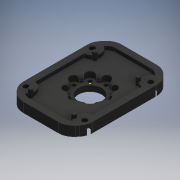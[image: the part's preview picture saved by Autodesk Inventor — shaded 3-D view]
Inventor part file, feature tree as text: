
AUTODESK INVENTOR PART (.ipt)
format: ipt  version: 2019 (Build 230136000, 136)  size: 553,984 bytes
history: native  units: mm
features: extrude x8, sketch x4, other x2, fillet x2, pattern_circular x2, shell x1, chamfer x1, pattern_linear x1
ambient origin geometry x8: Origin, YZ Plane, XZ Plane, XY Plane, X Axis, Y Axis, Z Axis, Center Point
bodies: Solid1 (feature_tree)
feature tree (21):
  other  "connector"
  sketch  "Sketch1"  dims[d1=20.0mm d3=20.0mm d4=30.0mm d5=17.0mm d6=5.0mm d7=0.0mm d8=8.0mm d9=22.0mm]
  extrude  "Extrusion1"  Depth=8.0mm
  fillet  "Fillet1"  Radius=22.0mm
  extrude  "Extrusion4"  Depth=3.0mm TaperAngle=0.0deg
  shell  "Shell2"  Thickness=0.5mm
  sketch  "Sketch2"  dims[d14=0.5mm d15=1.0mm d16=0.0mm]
  extrude  "Extrusion2"  Depth=1.0mm TaperAngle=0.0deg
  extrude  "Extrusion3"  Depth=8.25mm TaperAngle=0.0deg
  chamfer  "Chamfer1"  Distance=2.0mm
  sketch  "Sketch Driven Pattern1"  dims[d10=5.25mm d11=3.0mm d12=0.0mm d13=0.5mm]
  extrude  "Extrusion5"  Depth=8.25mm TaperAngle=0.0deg
  extrude  "Extrusion7"  Depth=8.25mm TaperAngle=360.0deg
  pattern_circular  "Circular Pattern1"  [2 undecoded]
  extrude  "Extrusion6"  Depth=8.25mm TaperAngle=0.0deg
  fillet  "Fillet2"  Radius=7.0mm
  pattern_linear  "Rectangular Pattern1"  Spacing1=3.0mm  [1 undecoded]
  extrude  "Extrusion8"  Depth=8.25mm
  pattern_circular  "Circular Pattern2"  [2 undecoded]
  other  "MeshFeature1"
  sketch  "Sketch3"  dims[d17=0.5mm d18=2.0mm d19=45.0deg d20=3.0mm d21=0.0mm d23=2.0mm d24=8.0mm d25=0.0mm d26=80.0mm d27=360.0deg d29=12.0mm d30=5.0mm d31=0.0mm d32=7.0mm d33=0.0mm d34=3.0mm d35=4.5mm d36=7.0mm d37=0.0mm d38=2.0mm d39=20.0mm d41=8.0mm d45=10.0mm d46=0.0mm d47=8.0mm d48=22.5deg d49=2.0mm d50=40.0mm d51=360.0deg d53=8.25mm]
note: 5 required parameter values undecoded (feature->parameter linkage not recoverable at this tier; creation-order binding heuristic only, values carry confidence <= 0.55)
